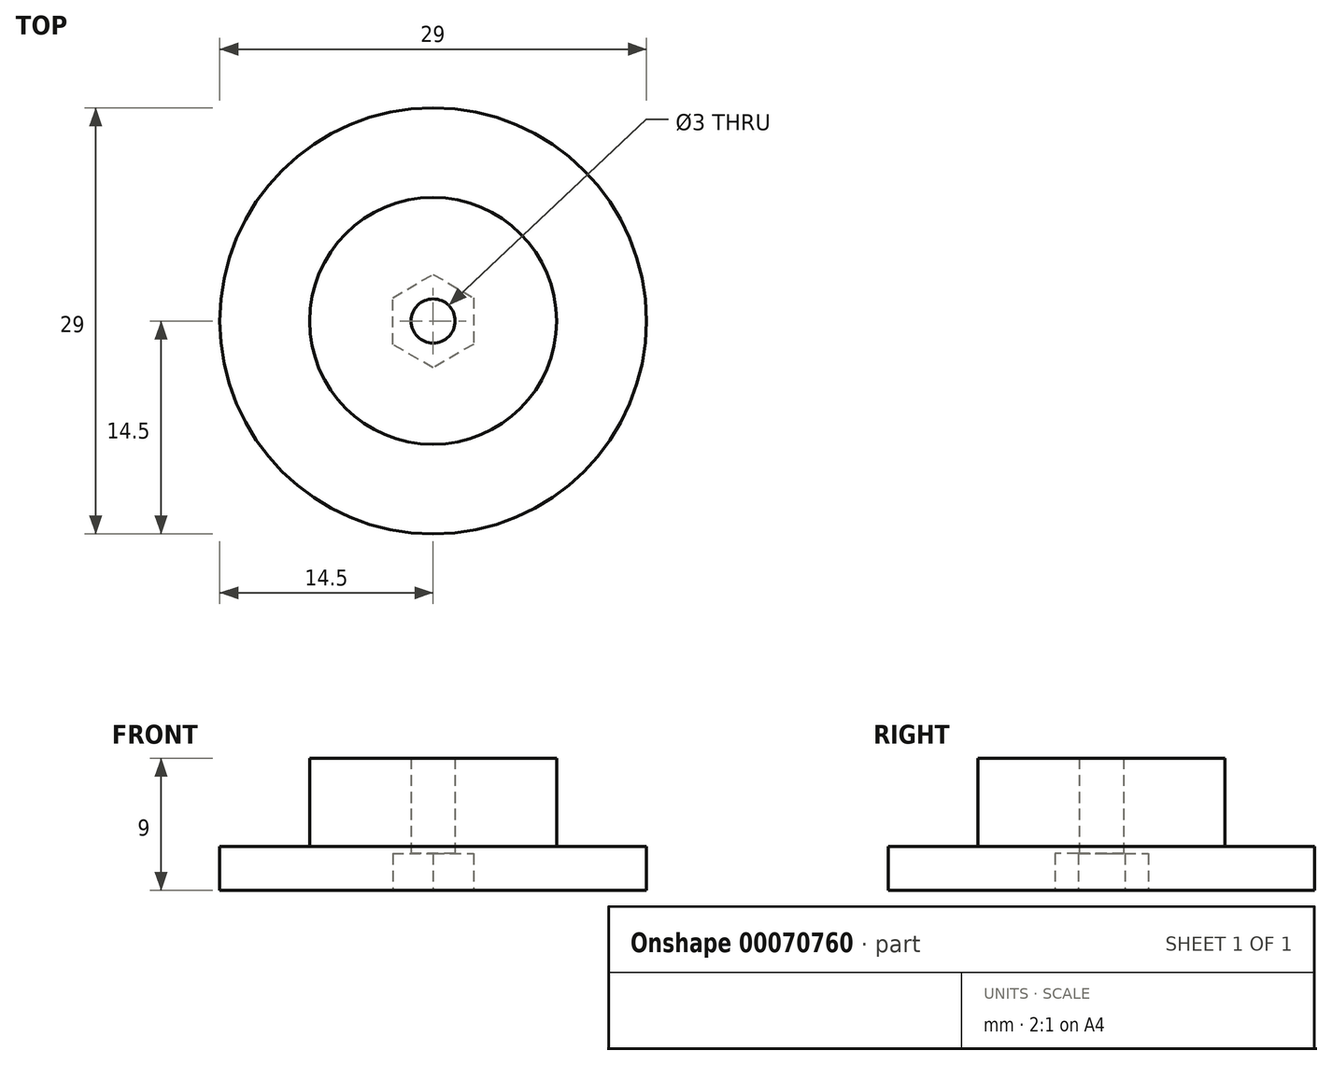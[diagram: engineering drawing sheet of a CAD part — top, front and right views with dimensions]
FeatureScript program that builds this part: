
annotation { "Feature Type Name" : "Feature", "Feature Type Description" : "" }
export const myFeature = defineFeature(function(context is Context, id is Id, definition is map)
    precondition{}
    {
        {
            var Q0;
            Q0=qCreatedBy(makeId("Top.planeOp"),FACE);
            var sketch = newSketch(context, id + "F0", { "sketchPlane" : qUnion([Q0])});
            skCircle(sketch, "E0", {"center": v(0, 0) * mm, "radius": 14.5 * mm});
            skCircle(sketch, "E1", {"center": v(0, 0) * mm, "radius": 8.4 * mm});
            skCircle(sketch, "E2", {"center": v(0, 0) * mm, "radius": 1.5 * mm});
            skCircle(sketch, "E3.cCircle", {"center": v(0, 0) * mm, "radius": 3.18 * mm, "construction": true});
            skLineSegment(sketch, "E3.0", {"start": v(-2.75, 1.59) * mm, "end": v(0, 3.18) * mm});
            skLineSegment(sketch, "E3.1", {"start": v(0, 3.18) * mm, "end": v(2.75, 1.59) * mm});
            skLineSegment(sketch, "E3.2", {"start": v(2.75, 1.59) * mm, "end": v(2.75, -1.59) * mm});
            skLineSegment(sketch, "E3.3", {"start": v(2.75, -1.59) * mm, "end": v(0, -3.18) * mm});
            skLineSegment(sketch, "E3.4", {"start": v(0, -3.18) * mm, "end": v(-2.75, -1.59) * mm});
            skLineSegment(sketch, "E3.5", {"start": v(-2.75, -1.59) * mm, "end": v(-2.75, 1.59) * mm});
            skSolve(sketch);
        }
        {
            var Q0;
            Q0=makeQuery(id+"F0.imprint","IMPRINT",FACE,{"disambiguationData":[TD([[makeQuery(id+"F0.imprint","IMPRINT",EDGE,{"derivedFrom":sQuery(id+"F0.wireOp",EDGE,"E0")}),1.0]])]});
            extrude(context, id + "F1", {"entities" : qUnion([Q0]), "depth" : 3 * mm});
        }
        {
            var Q0;
            Q0=makeQuery(id+"F0.imprint","IMPRINT",FACE,{"disambiguationData":[TD([[makeQuery(id+"F0.imprint","IMPRINT",EDGE,{"derivedFrom":sQuery(id+"F0.wireOp",EDGE,"E1")}),1.0]])]});
            extrude(context, id + "F2", {"entities" : qUnion([Q0]), "operationType" : NewBodyOperationType.ADD, "depth" : 9 * mm});
        }
        {
            var Q0;
            Q0=makeQuery(id+"F0.imprint","IMPRINT",FACE,{"disambiguationData":[TD([[makeQuery(id+"F0.imprint","IMPRINT",EDGE,{"derivedFrom":sQuery(id+"F0.wireOp",EDGE,"E2")}),-1.0]])]});
            var Q1;
            Q1=sQuery(id+"F0.wireOp",EDGE,"E3.0");
            var Q2;
            Q2=sQuery(id+"F0.wireOp",EDGE,"E3.5");
            var Q3;
            Q3=sQuery(id+"F0.wireOp",EDGE,"E3.4");
            var Q4;
            Q4=sQuery(id+"F0.wireOp",EDGE,"E3.3");
            var Q5;
            Q5=sQuery(id+"F0.wireOp",EDGE,"E3.2");
            var Q6;
            Q6=sQuery(id+"F0.wireOp",EDGE,"E3.1");
            var Q7;
            Q7=sQuery(id+"F0.wireOp",EDGE,"E2");
            extrude(context, id + "F3", {"entities" : qUnion([Q0]), "operationType" : NewBodyOperationType.ADD, "surfaceEntities" : qUnion([Q1, Q2, Q3, Q4, Q5, Q6, Q7]), "depth" : 9 * mm, "hasSecondDirection" : true, "secondDirectionOppositeDirection" : false, "secondDirectionDepth" : 2.5 * mm});
        }
    });
